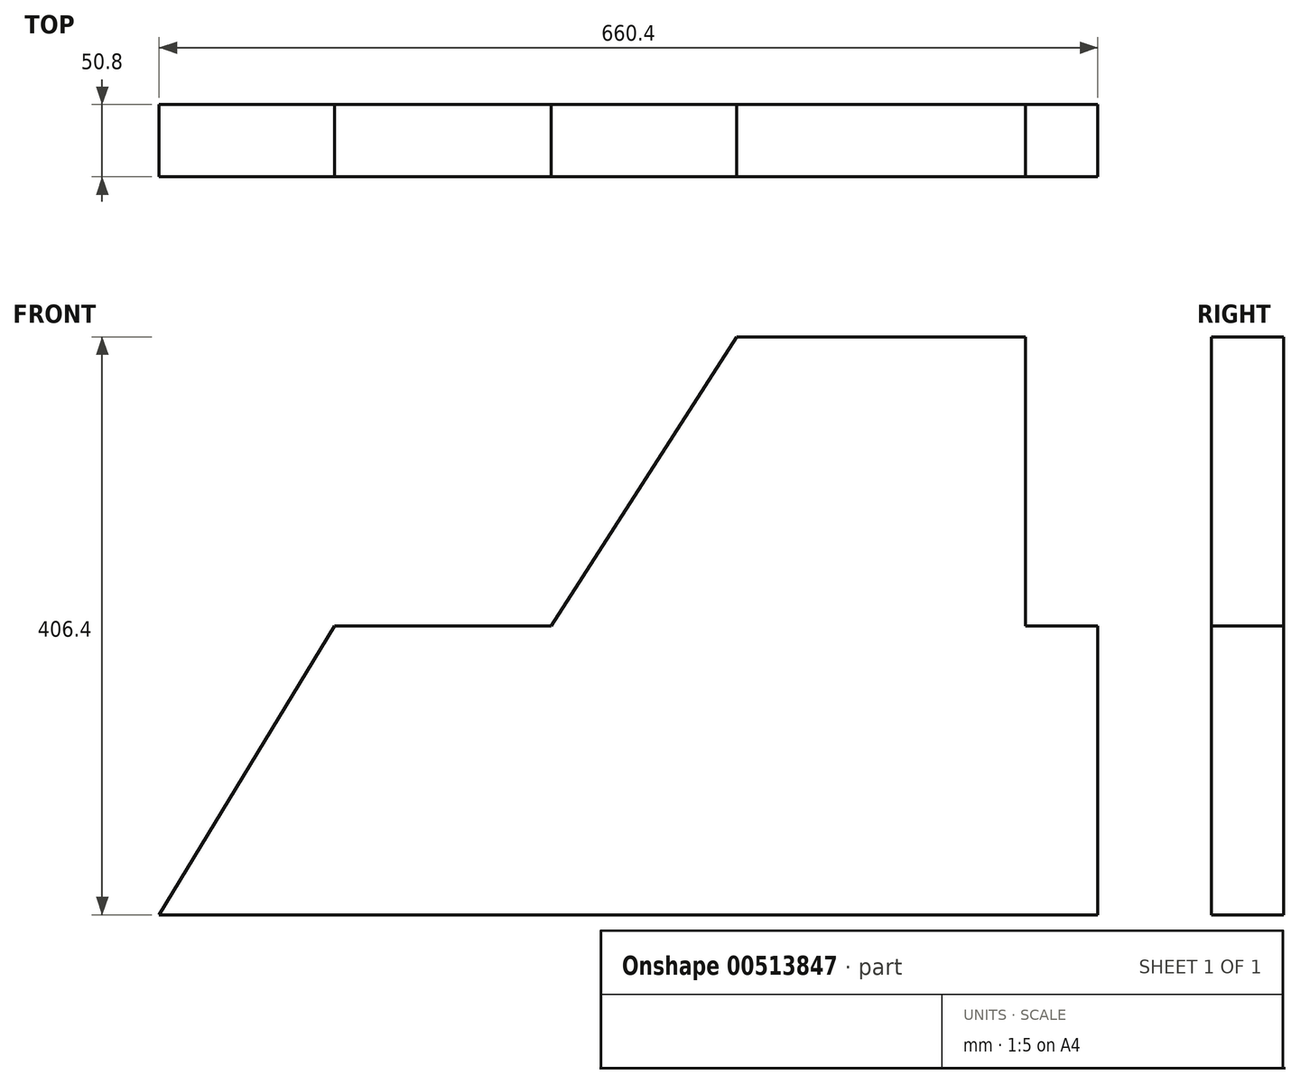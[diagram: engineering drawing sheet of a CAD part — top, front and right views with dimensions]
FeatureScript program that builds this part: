
annotation { "Feature Type Name" : "Feature", "Feature Type Description" : "" }
export const myFeature = defineFeature(function(context is Context, id is Id, definition is map)
    precondition{}
    {
        {
            var Q0;
            Q0=qCreatedBy(makeId("Front.planeOp"),FACE);
            var sketch = newSketch(context, id + "F0", { "sketchPlane" : qUnion([Q0])});
            skLineSegment(sketch, "E0", {"start": v(0, 0) * mm, "end": v(660.4, 0) * mm});
            skLineSegment(sketch, "E1", {"start": v(660.4, 0) * mm, "end": v(660.4, 203.2) * mm});
            skLineSegment(sketch, "E2", {"start": v(660.4, 203.2) * mm, "end": v(609.6, 203.2) * mm});
            skLineSegment(sketch, "E3", {"start": v(609.6, 203.2) * mm, "end": v(609.6, 406.4) * mm});
            skLineSegment(sketch, "E4", {"start": v(609.6, 406.4) * mm, "end": v(406.4, 406.4) * mm});
            skLineSegment(sketch, "E5", {"start": v(406.4, 406.4) * mm, "end": v(275.82, 203.2) * mm});
            skLineSegment(sketch, "E6", {"start": v(275.82, 203.2) * mm, "end": v(123.42, 203.2) * mm});
            skLineSegment(sketch, "E7", {"start": v(123.42, 203.2) * mm, "end": v(0, 0) * mm});
            skSolve(sketch);
        }
        {
            var Q0;
            Q0=makeQuery(id+"F0.imprint","IMPRINT",FACE,{"disambiguationData":[TD([[makeQuery(id+"F0.imprint","IMPRINT",EDGE,{"derivedFrom":sQuery(id+"F0.wireOp",EDGE,"E0")}),1.0]])]});
            extrude(context, id + "F1", {"entities" : qUnion([Q0]), "depth" : 50.8 * mm, "offsetDistance" : 25.4 * mm});
        }
    });
